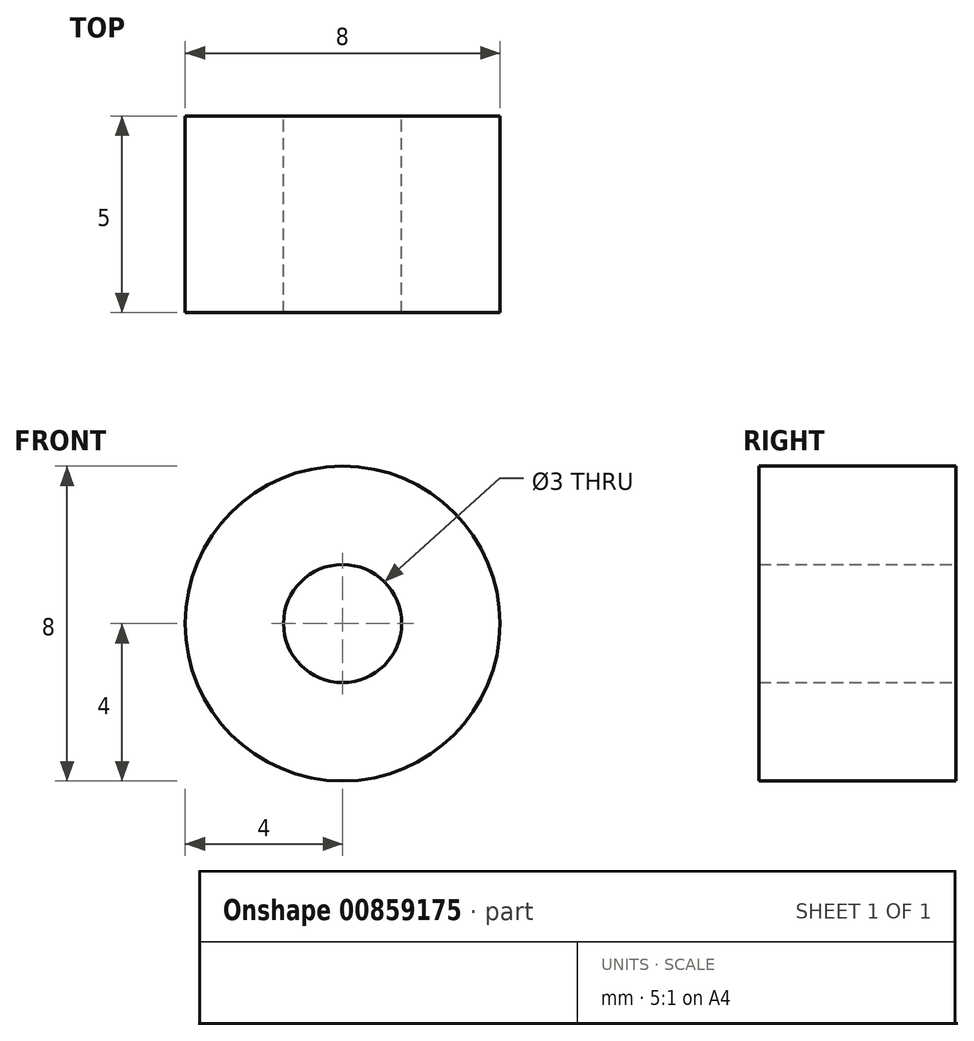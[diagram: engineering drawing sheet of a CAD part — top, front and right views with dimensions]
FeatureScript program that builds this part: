
annotation { "Feature Type Name" : "Feature", "Feature Type Description" : "" }
export const myFeature = defineFeature(function(context is Context, id is Id, definition is map)
    precondition{}
    {
        {
            var Q0;
            Q0=qCreatedBy(makeId("Front.planeOp"),FACE);
            var sketch = newSketch(context, id + "F0", { "sketchPlane" : qUnion([Q0])});
            skCircle(sketch, "E0", {"center": v(0, 0) * mm, "radius": 1.5 * mm});
            skCircle(sketch, "E1", {"center": v(0, 0) * mm, "radius": 4 * mm});
            skSolve(sketch);
        }
        {
            var Q0;
            Q0=makeQuery(id+"F0.imprint","IMPRINT",FACE,{"disambiguationData":[TD([[makeQuery(id+"F0.imprint","IMPRINT",EDGE,{"derivedFrom":sQuery(id+"F0.wireOp",EDGE,"E0")}),-1.0]])]});
            extrude(context, id + "F1", {"entities" : qUnion([Q0]), "depth" : 5 * mm, "offsetDistance" : 25 * mm});
        }
    });
